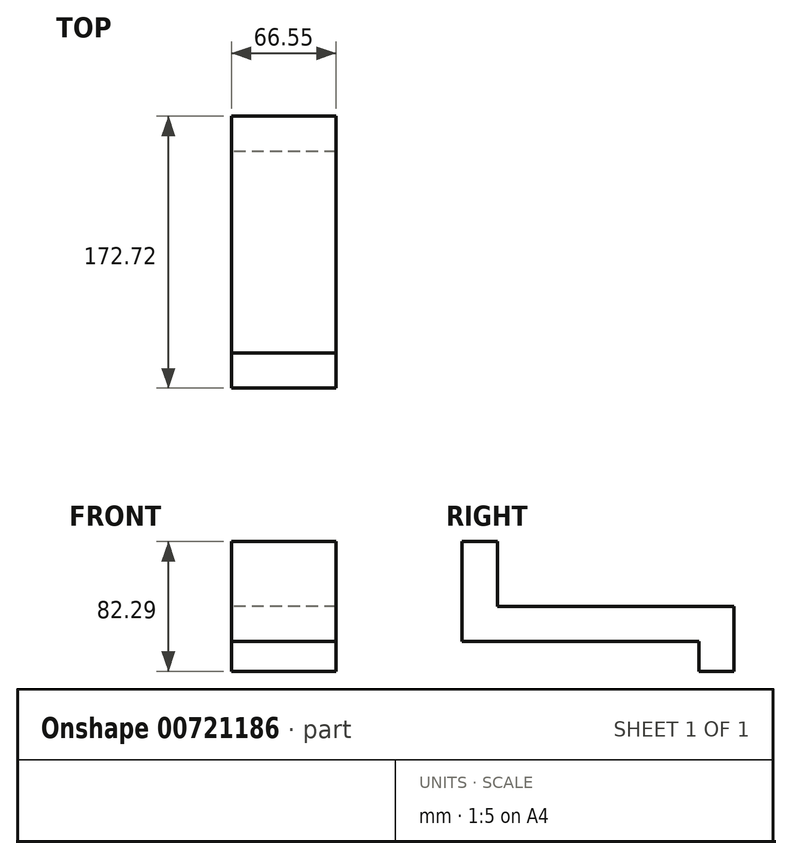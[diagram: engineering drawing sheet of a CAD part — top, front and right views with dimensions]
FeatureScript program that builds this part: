
annotation { "Feature Type Name" : "Feature", "Feature Type Description" : "" }
export const myFeature = defineFeature(function(context is Context, id is Id, definition is map)
    precondition{}
    {
        {
            var Q0;
            Q0=qCreatedBy(makeId("Right.planeOp"),FACE);
            var sketch = newSketch(context, id + "F0", { "sketchPlane" : qUnion([Q0])});
            skLineSegment(sketch, "E0.bottom", {"start": v(-68.18, 47.66) * mm, "end": v(-45.82, 47.66) * mm});
            skLineSegment(sketch, "E0.top", {"start": v(-68.18, -15.84) * mm, "end": v(-45.82, -15.84) * mm});
            skLineSegment(sketch, "E0.left", {"start": v(-68.18, 47.66) * mm, "end": v(-68.18, -15.84) * mm});
            skLineSegment(sketch, "E0.right", {"start": v(-45.82, 47.66) * mm, "end": v(-45.82, 6.52) * mm});
            skLineSegment(sketch, "E1.bottom", {"start": v(-45.82, -15.84) * mm, "end": v(82.2, -15.84) * mm});
            skLineSegment(sketch, "E1.top", {"start": v(-45.82, 6.52) * mm, "end": v(82.2, 6.52) * mm});
            skLineSegment(sketch, "E2.right", {"start": v(104.82, 6.52) * mm, "end": v(104.82, 3.57) * mm});
            skLineSegment(sketch, "E3.bottom", {"start": v(82.2, 6.52) * mm, "end": v(104.54, 6.52) * mm});
            skLineSegment(sketch, "E3.top", {"start": v(82.2, -34.63) * mm, "end": v(104.54, -34.63) * mm});
            skLineSegment(sketch, "E3.right", {"start": v(104.54, 6.52) * mm, "end": v(104.54, -34.63) * mm});
            skLineSegment(sketch, "E4.trimOffspring", {"start": v(82.2, -15.84) * mm, "end": v(82.2, -34.63) * mm});
            skSolve(sketch);
        }
        {
            var Q0;
            Q0=makeQuery(id+"F0.imprint","IMPRINT",FACE,{"disambiguationData":[TD([[makeQuery(id+"F0.imprint","IMPRINT",EDGE,{"derivedFrom":sQuery(id+"F0.wireOp",EDGE,"E0.bottom")}),-1.0]])]});
            extrude(context, id + "F1", {"entities" : qUnion([Q0]), "depth" : 66.55 * mm, "offsetDistance" : 25.4 * mm});
        }
    });
